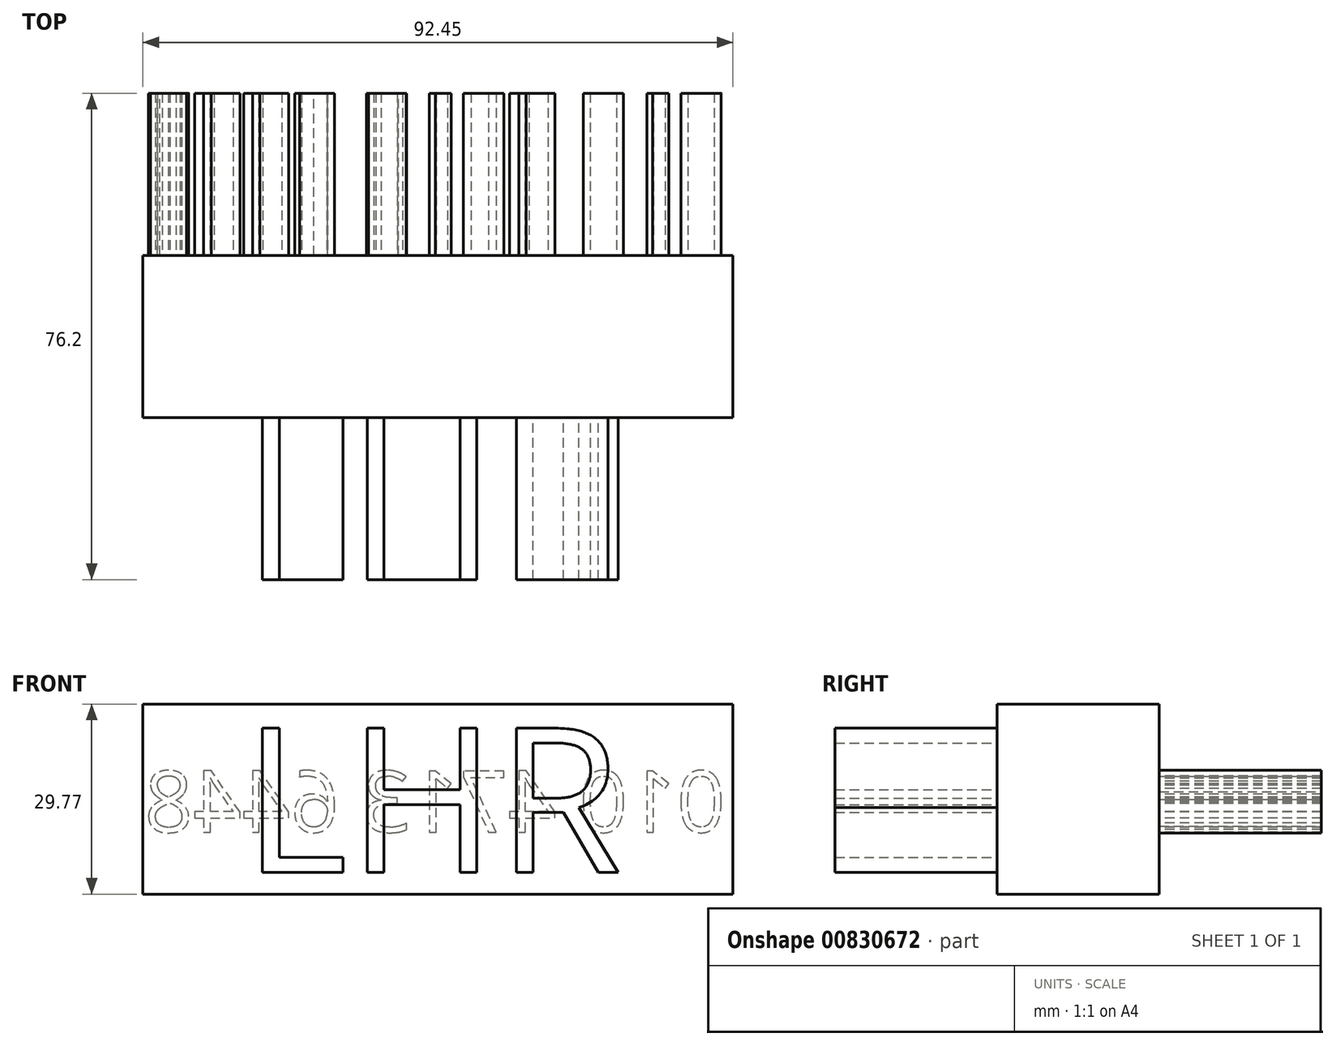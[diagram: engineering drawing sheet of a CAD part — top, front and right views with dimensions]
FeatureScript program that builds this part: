
annotation { "Feature Type Name" : "Feature", "Feature Type Description" : "" }
export const myFeature = defineFeature(function(context is Context, id is Id, definition is map)
    precondition{}
    {
        {
            var Q0;
            Q0=qCreatedBy(makeId("Front.planeOp"),FACE);
            var sketch = newSketch(context, id + "F0", { "sketchPlane" : qUnion([Q0])});
            skLineSegment(sketch, "E0.bottom", {"start": v(0, 29.77) * mm, "end": v(92.45, 29.77) * mm});
            skLineSegment(sketch, "E0.top", {"start": v(0, 0) * mm, "end": v(92.45, 0) * mm});
            skLineSegment(sketch, "E0.left", {"start": v(0, 29.77) * mm, "end": v(0, 0) * mm});
            skLineSegment(sketch, "E0.right", {"start": v(92.45, 29.77) * mm, "end": v(92.45, 0) * mm});
            skSolve(sketch);
        }
        {
            var Q0;
            Q0=makeQuery(id+"F0.imprint","IMPRINT",FACE,{"disambiguationData":[TD([[makeQuery(id+"F0.imprint","IMPRINT",EDGE,{"derivedFrom":sQuery(id+"F0.wireOp",EDGE,"E0.bottom")}),-1.0]])]});
            extrude(context, id + "F1", {"entities" : qUnion([Q0]), "depth" : 25.4 * mm, "offsetDistance" : 25.4 * mm});
        }
        {
            var Q0;
            Q0=makeQuery(id+"F1.opExtrude","CAP_FACE",FACE,{"disambiguationData":[OSD([sQuery(id+"F0.wireOp",EDGE,"E0.bottom"),sQuery(id+"F0.wireOp",EDGE,"E0.top"),sQuery(id+"F0.wireOp",EDGE,"E0.left"),sQuery(id+"F0.wireOp",EDGE,"E0.right")])],"isStart":false});
            var sketch = newSketch(context, id + "F2", { "sketchPlane" : qUnion([Q0])});
            skText(sketch, "E1", { "text": "LHR", "fontName": "OpenSans-Regular.ttf"});
            const initialGuessF2  = {"E1": [0.01562, 0.00338, 1, 0, 0.0228]};
            skSetInitialGuess(sketch, initialGuessF2);
            skSolve(sketch);
        }
        {
            var Q0;
            Q0 = qSketchRegion(id + "F2", true);
            extrude(context, id + "F3", {"entities" : qUnion([Q0]), "operationType" : NewBodyOperationType.ADD, "depth" : 25.4 * mm, "offsetDistance" : 25.4 * mm});
        }
        {
            var Q0;
            Q0=makeQuery(id+"F1.opExtrude","CAP_FACE",FACE,{"disambiguationData":[OSD([sQuery(id+"F0.wireOp",EDGE,"E0.bottom"),sQuery(id+"F0.wireOp",EDGE,"E0.top"),sQuery(id+"F0.wireOp",EDGE,"E0.left"),sQuery(id+"F0.wireOp",EDGE,"E0.right")])],"isStart":true});
            var sketch = newSketch(context, id + "F4", { "sketchPlane" : qUnion([Q0])});
            skSolve(sketch);
        }
        {
            var Q0;
            Q0=makeQuery(id+"F4.imprint","IMPRINT",FACE,{"disambiguationData":[TD([[makeQuery(id+"F4.imprint","IMPRINT",EDGE,{"derivedFrom":makeQuery(id+"F1.opExtrude","CAP_EDGE",EDGE,{"disambiguationData":[OSD([sQuery(id+"F0.wireOp",EDGE,"E0.bottom")])],"isStart":true})}),1.0]])]});
            var sketch = newSketch(context, id + "F5", { "sketchPlane" : qUnion([Q0])});
            skText(sketch, "E2", { "text": "010 4713 6448", "fontName": "OpenSans-Regular.ttf"});
            const initialGuessF5  = {"E2": [-0.09127, 0.00972, 1, 0, 0.00963]};
            skSetInitialGuess(sketch, initialGuessF5);
            skSolve(sketch);
        }
        {
            var Q0;
            Q0 = qSketchRegion(id + "F5", true);
            extrude(context, id + "F6", {"entities" : qUnion([Q0]), "operationType" : NewBodyOperationType.ADD, "depth" : 25.4 * mm, "offsetDistance" : 25.4 * mm});
        }
    });
